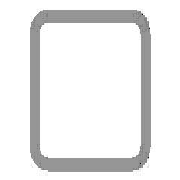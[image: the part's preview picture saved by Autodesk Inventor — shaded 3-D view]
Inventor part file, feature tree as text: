
AUTODESK INVENTOR PART (.ipt)
format: ipt  version: 2024 (Build 280153000, 153)  size: 135,168 bytes
history: native  units: mm (DEFAULTED — no unit token found)
features: other x4, plane x2, extrude x1, split x1, sketch x1
ambient origin geometry x8: Origin, YZ Plane, XZ Plane, XY Plane, X Axis, Y Axis, Z Axis, Center Point
bodies: Solid1 (feature_tree)
feature tree (9):
  parser-record x1  (decoder bookkeeping rows leaked as tree rows — omitted from the tree; the rows remain in map.json)
  other  "Driven Length"
  other  "Plano inicial"
  other  "Plano final"
  extrude  "Cuerpo"  TaperAngle=0.0deg  [1 undecoded]
  plane  "Plano de trabajo4"
  split  "Dividir1"
  sketch  "Sketch3"  dims[d3=374.6mm d4=0.0mm d10=50.8mm d11=50.8mm d12=3.175mm d13=-0.0mm d14=374.6mm d15=25.4mm d16=25.4mm d17=6.35mm d18=90.0deg d19=374.6mm]
  plane  "Work Plane3"
note: 1 required parameter value undecoded (feature->parameter linkage not recoverable at this tier; creation-order binding heuristic only, values carry confidence <= 0.55)
